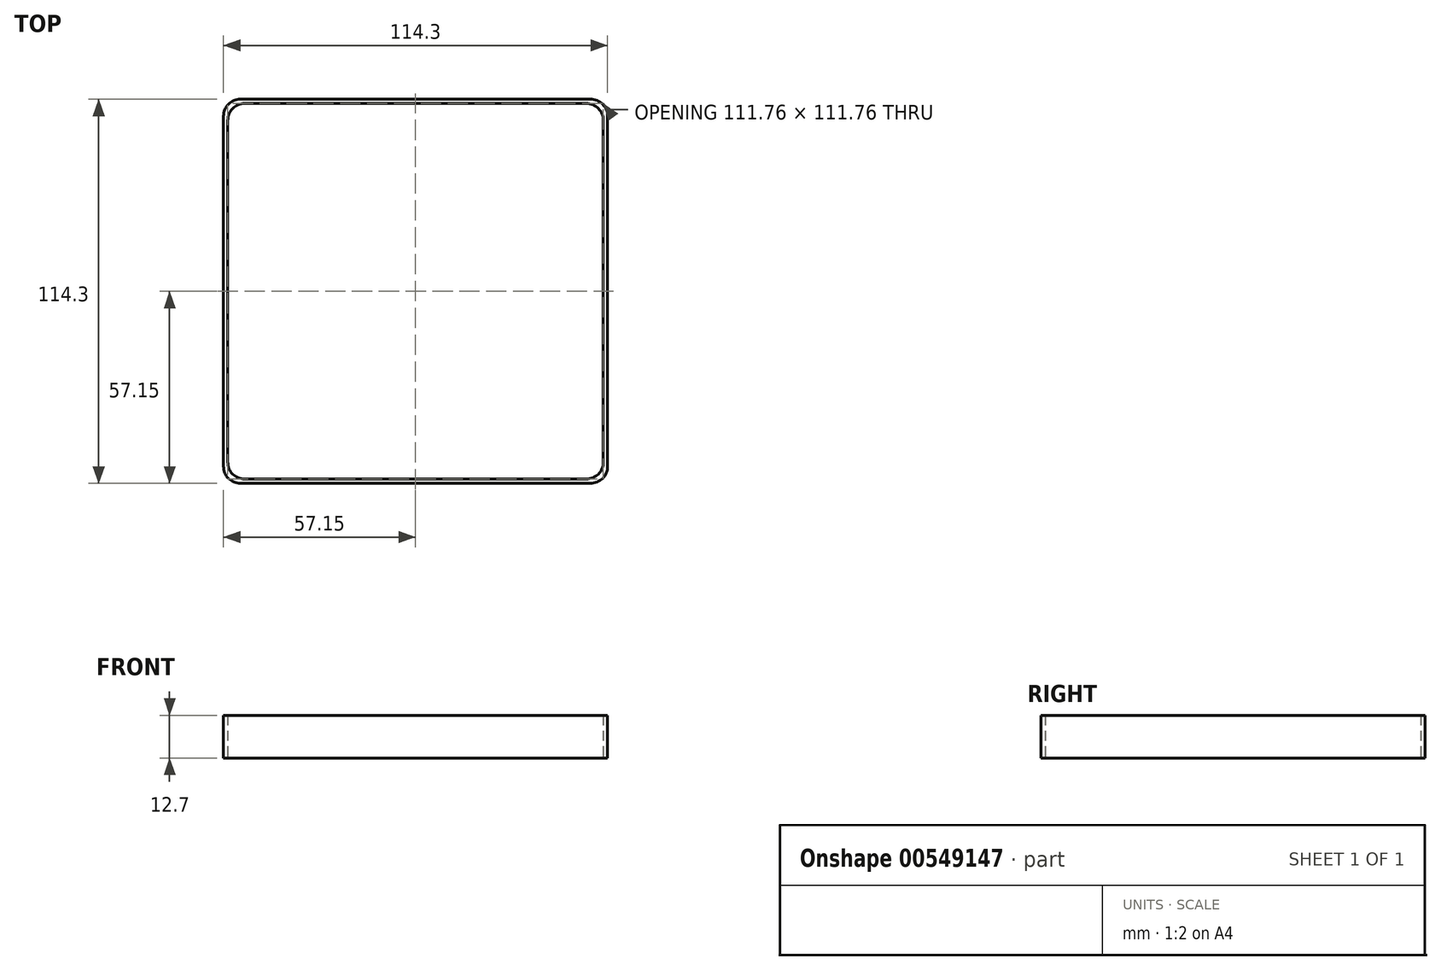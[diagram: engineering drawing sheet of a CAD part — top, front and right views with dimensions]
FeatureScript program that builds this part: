
annotation { "Feature Type Name" : "Feature", "Feature Type Description" : "" }
export const myFeature = defineFeature(function(context is Context, id is Id, definition is map)
    precondition{}
    {
        {
            var Q0;
            Q0=qCreatedBy(makeId("Top.planeOp"),FACE);
            var sketch = newSketch(context, id + "F0", { "sketchPlane" : qUnion([Q0])});
            skLineSegment(sketch, "E0.bottom", {"start": v(57.15, -57.15) * mm, "end": v(-57.15, -57.15) * mm});
            skLineSegment(sketch, "E0.top", {"start": v(57.15, 57.15) * mm, "end": v(-57.15, 57.15) * mm});
            skLineSegment(sketch, "E0.left", {"start": v(57.15, -57.15) * mm, "end": v(57.15, 57.15) * mm});
            skLineSegment(sketch, "E0.right", {"start": v(-57.15, -57.15) * mm, "end": v(-57.15, 57.15) * mm});
            skPoint(sketch, "E0.middle", {"position": v(0, 0) * mm});
            skLineSegment(sketch, "E1.0", {"start": v(55.88, 55.88) * mm, "end": v(-55.88, 55.88) * mm});
            skLineSegment(sketch, "E1.1", {"start": v(55.88, -55.88) * mm, "end": v(55.88, 55.88) * mm});
            skLineSegment(sketch, "E1.2", {"start": v(55.88, -55.88) * mm, "end": v(-55.88, -55.88) * mm});
            skLineSegment(sketch, "E1.3", {"start": v(-55.88, -55.88) * mm, "end": v(-55.88, 55.88) * mm});
            skSolve(sketch);
        }
        {
            var Q0;
            Q0=makeQuery(id+"F0.imprint","IMPRINT",FACE,{"disambiguationData":[TD([[makeQuery(id+"F0.imprint","IMPRINT",EDGE,{"derivedFrom":sQuery(id+"F0.wireOp",EDGE,"E0.bottom")}),-1.0]])]});
            extrude(context, id + "F1", {"entities" : qUnion([Q0]), "depth" : 12.7 * mm, "offsetDistance" : 25.4 * mm});
        }
        {
            var Q0;
            Q0=makeQuery(id+"F1.opExtrude","SWEPT_EDGE",EDGE,{"disambiguationData":[OSD([sQuery(id+"F0.wireOp",EDGE,"E0.bottom"),sQuery(id+"F0.wireOp",EDGE,"E0.right")])]});
            var Q1;
            Q1=makeQuery(id+"F1.opExtrude","SWEPT_EDGE",EDGE,{"disambiguationData":[OSD([sQuery(id+"F0.wireOp",EDGE,"E0.bottom"),sQuery(id+"F0.wireOp",EDGE,"E0.left")])]});
            var Q2;
            Q2=makeQuery(id+"F1.opExtrude","SWEPT_EDGE",EDGE,{"disambiguationData":[OSD([sQuery(id+"F0.wireOp",EDGE,"E0.top"),sQuery(id+"F0.wireOp",EDGE,"E0.left")])]});
            var Q3;
            Q3=makeQuery(id+"F1.opExtrude","SWEPT_EDGE",EDGE,{"disambiguationData":[OSD([sQuery(id+"F0.wireOp",EDGE,"E0.top"),sQuery(id+"F0.wireOp",EDGE,"E0.right")])]});
            var Q4;
            Q4=makeQuery(id+"F1.opExtrude","SWEPT_EDGE",EDGE,{"disambiguationData":[OSD([sQuery(id+"F0.wireOp",EDGE,"E1.0"),sQuery(id+"F0.wireOp",EDGE,"E1.1")])]});
            var Q5;
            Q5=makeQuery(id+"F1.opExtrude","SWEPT_EDGE",EDGE,{"disambiguationData":[OSD([sQuery(id+"F0.wireOp",EDGE,"E1.0"),sQuery(id+"F0.wireOp",EDGE,"E1.3")])]});
            var Q6;
            Q6=makeQuery(id+"F1.opExtrude","SWEPT_EDGE",EDGE,{"disambiguationData":[OSD([sQuery(id+"F0.wireOp",EDGE,"E1.2"),sQuery(id+"F0.wireOp",EDGE,"E1.3")])]});
            var Q7;
            Q7=makeQuery(id+"F1.opExtrude","SWEPT_EDGE",EDGE,{"disambiguationData":[OSD([sQuery(id+"F0.wireOp",EDGE,"E1.1"),sQuery(id+"F0.wireOp",EDGE,"E1.2")])]});
            fillet(context, id + "F2", {"entities" : qUnion([Q0, Q1, Q2, Q3, Q4, Q5, Q6, Q7]), "radius" : 5.08 * mm, "tangentPropagation" : true, "allowEdgeOverflow" : false});
        }
    });
